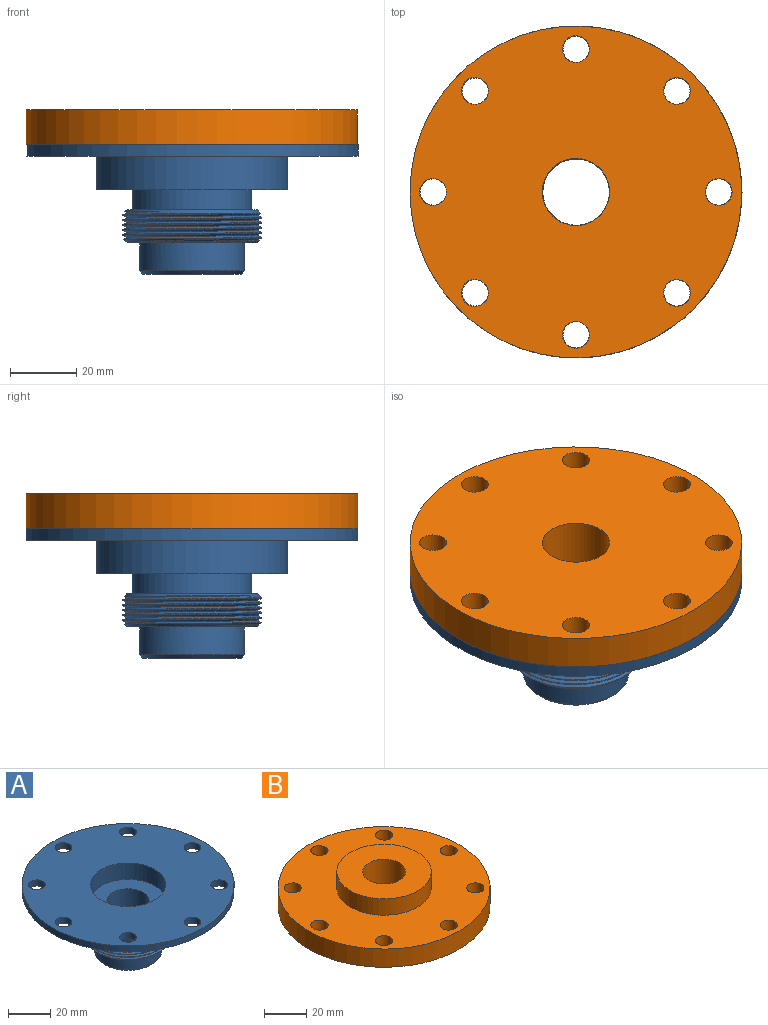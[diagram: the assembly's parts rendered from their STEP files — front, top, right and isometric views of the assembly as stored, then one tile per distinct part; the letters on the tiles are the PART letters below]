
ASSEMBLY  parts=2 mates=1
PART A: 28 faces, bbox 100x100x39 mm
  f0: cone r=20.87mm half-angle=45deg, axis (0,0,-1), area 164.5mm2, adj f7,f9,f11,f13
  f1: cylinder r=50mm len=100mm, axis (0,0,1), area 1099.6mm2, adj f2,f3
  f2: plane 100x100mm, normal (0,0,-1), area 4856.1mm2, adj f1,f4,f19,f20,f21,f22,f23,f24
  f3: plane 100x100mm, normal (0,0,1), area 6472.1mm2, adj f1,f16,f19,f20,f21,f22,f23,f24
  f4: cylinder r=28.8mm len=57.6mm, axis (0,0,1), area 1809.6mm2, adj f2,f5
  f5: plane 57.6x57.6mm, normal (0,0,-1), area 1587.9mm2, adj f4,f6
  f6: cylinder r=18mm len=36mm, axis (0,0,1), area 689.9mm2, adj f5,f9
  f7: cylinder r=20.87mm len=41.73mm, axis (0,0,1), area 164.2mm2, adj f0,f10,f11,f12,f13
  f8: plane 39.23x39.23mm, normal (0,0,-1), area 424.6mm2, adj f10,f14
  f9: plane 39.23x39.23mm, normal (0,0,1), area 191mm2, adj f0,f6
  f10: cone r=19.62mm half-angle=45deg, axis (0,0,1), area 142.8mm2, adj f7,f8,f12,f13
  f11: plane 0.94x0.79mm, normal (-0.87,0.5,0), area 0.2mm2, adj f0,f7,f12,f13
  f12: bspline ~48.19x41.73mm, area 888.6mm2, adj f7,f10,f11,f13
  f13: bspline ~48.19x41.73mm, area 905.4mm2, adj f0,f7,f10,f11,f12
  f14: cylinder r=15.8mm len=31.6mm, axis (0,0,1), area 833.9mm2, adj f8,f27
  f15: plane 29.6x29.6mm, normal (0,0,-1), area 374mm2, adj f18,f27
  f16: cylinder r=17.75mm len=35.5mm, axis (0,0,1), area 1048.3mm2, adj f3,f17
  f17: plane 35.5x35.5mm, normal (0,0,1), area 675.6mm2, adj f16,f18
  f18: cylinder r=10mm len=29.6mm, axis (0,0,-1), area 1859.8mm2, adj f15,f17
  f19: cylinder r=3.95mm len=7.9mm, axis (0,0,1), area 86.9mm2, adj f2,f3
  f20: cylinder r=3.95mm len=7.9mm, axis (0,0,1), area 86.9mm2, adj f2,f3
  f21: cylinder r=3.95mm len=7.9mm, axis (0,0,1), area 86.9mm2, adj f2,f3
  f22: cylinder r=3.95mm len=7.9mm, axis (0,0,1), area 86.9mm2, adj f2,f3
  f23: cylinder r=3.95mm len=7.9mm, axis (0,0,1), area 86.9mm2, adj f2,f3
  f24: cylinder r=3.95mm len=7.9mm, axis (0,0,1), area 86.9mm2, adj f2,f3
  f25: cylinder r=3.95mm len=7.9mm, axis (0,0,1), area 86.9mm2, adj f2,f3
  f26: cylinder r=3.95mm len=7.9mm, axis (0,0,1), area 86.9mm2, adj f2,f3
  f27: cone r=14.8mm half-angle=45deg, axis (0,0,1), area 136mm2, adj f14,f15
PART B: 14 faces, bbox 100x100x19.9 mm
  f0: cylinder r=50mm len=100mm, axis (0,0,-1), area 3298.7mm2, adj f1,f2
  f1: plane 100x100mm, normal (0,0,1), area 5879.5mm2, adj f0,f3,f5,f6,f7,f8,f9,f10
  f2: plane 100x100mm, normal (0,0,-1), area 7120.3mm2, adj f0,f5,f6,f7,f8,f9,f10,f11
  f3: cylinder r=22.3mm len=44.6mm, axis (0,0,-1), area 1317.1mm2, adj f1,f4
  f4: plane 44.6x44.6mm, normal (0,0,1), area 1240.9mm2, adj f3,f13
  f5: cylinder r=4.05mm len=10.5mm, axis (0,0,1), area 267.2mm2, adj f1,f2
  f6: cylinder r=4.05mm len=10.5mm, axis (0,0,1), area 267.2mm2, adj f1,f2
  f7: cylinder r=4.05mm len=10.5mm, axis (0,0,1), area 267.2mm2, adj f1,f2
  f8: cylinder r=4.05mm len=10.5mm, axis (0,0,1), area 267.2mm2, adj f1,f2
  f9: cylinder r=4.05mm len=10.5mm, axis (0,0,1), area 267.2mm2, adj f1,f2
  f10: cylinder r=4.05mm len=10.5mm, axis (0,0,1), area 267.2mm2, adj f1,f2
  f11: cylinder r=4.05mm len=10.5mm, axis (0,0,1), area 267.2mm2, adj f1,f2
  f12: cylinder r=4.05mm len=10.5mm, axis (0,0,1), area 267.2mm2, adj f1,f2
  f13: cylinder r=10.12mm len=20.23mm, axis (0,0,1), area 1264.7mm2, adj f2,f4
PLACE A t=(-23.62,18.79,-25.69)mm
PLACE B rot(axis=(0,1,0),180deg) t=(-23.68,18.79,-15.19)mm
MATE slider A.f22 <-> B.f11  axis (0,0,1) through (19.38,18.79,-25.69)mm
